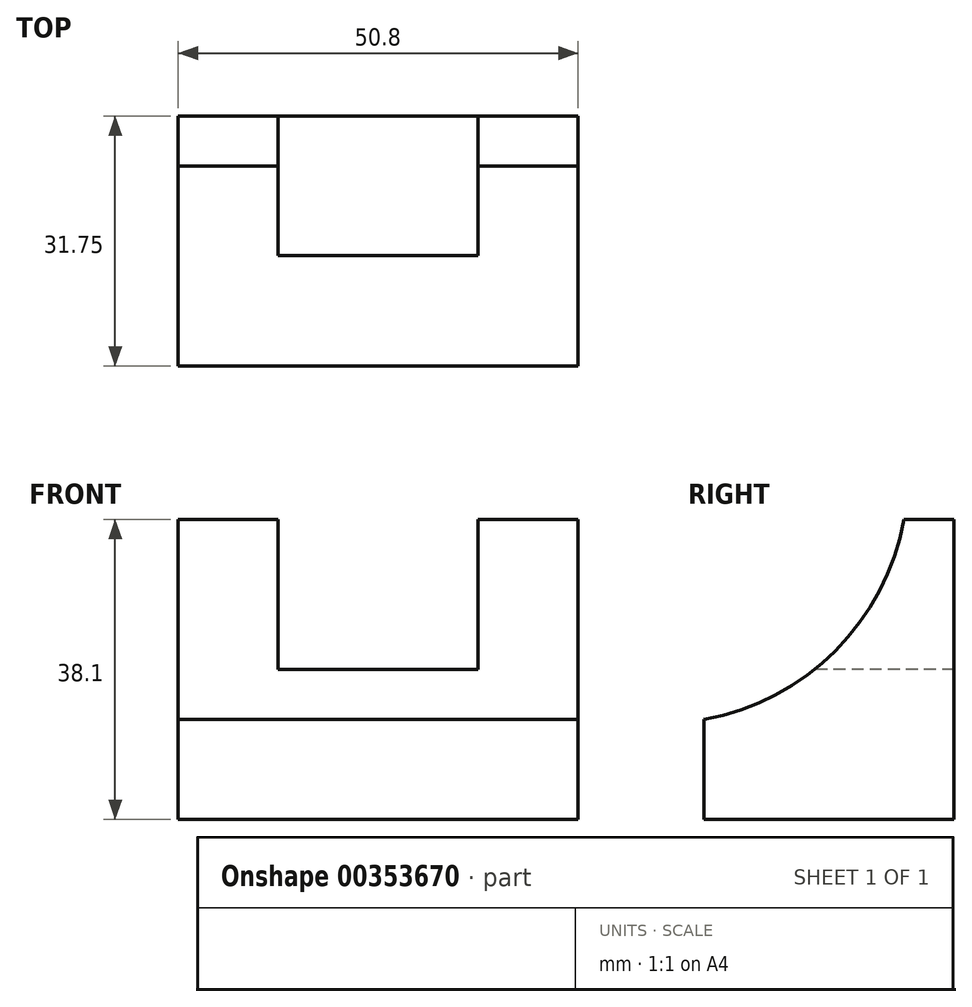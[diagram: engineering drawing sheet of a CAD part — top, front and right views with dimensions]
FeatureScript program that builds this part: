
annotation { "Feature Type Name" : "Feature", "Feature Type Description" : "" }
export const myFeature = defineFeature(function(context is Context, id is Id, definition is map)
    precondition{}
    {
        {
            var Q0;
            Q0=qCreatedBy(makeId("Right.planeOp"),FACE);
            var sketch = newSketch(context, id + "F0", { "sketchPlane" : qUnion([Q0])});
            skLineSegment(sketch, "E0", {"start": v(-28.04, 18.9) * mm, "end": v(-28.04, -19.2) * mm});
            skLineSegment(sketch, "E1", {"start": v(-28.04, -19.2) * mm, "end": v(3.71, -19.2) * mm});
            skLineSegment(sketch, "E2", {"start": v(3.71, -19.2) * mm, "end": v(3.71, 18.9) * mm});
            skLineSegment(sketch, "E3", {"start": v(3.71, 18.9) * mm, "end": v(-28.04, 18.9) * mm});
            skSolve(sketch);
        }
        {
            var Q0;
            Q0=makeQuery(id+"F0.imprint","IMPRINT",FACE,{"disambiguationData":[TD([[makeQuery(id+"F0.imprint","IMPRINT",EDGE,{"derivedFrom":sQuery(id+"F0.wireOp",EDGE,"E0")}),1.0]])]});
            extrude(context, id + "F1", {"entities" : qUnion([Q0]), "depth" : 50.8 * mm});
        }
        {
            var Q0;
            Q0=makeQuery(id+"F1.opExtrude","SWEPT_FACE",FACE,{"disambiguationData":[OSD([sQuery(id+"F0.wireOp",EDGE,"E0")])]});
            var sketch = newSketch(context, id + "F2", { "sketchPlane" : qUnion([Q0])});
            skLineSegment(sketch, "E4", {"start": v(12.7, 18.9) * mm, "end": v(12.7, -0.14) * mm});
            skLineSegment(sketch, "E5", {"start": v(12.7, -0.14) * mm, "end": v(38.1, -0.14) * mm});
            skLineSegment(sketch, "E6", {"start": v(38.1, -0.14) * mm, "end": v(38.1, 18.9) * mm});
            skSolve(sketch);
        }
        {
            var Q0;
            Q0 = qSketchRegion(id + "F2", true);
            var Q1;
            {var subQ0=sQuery(id+"F2.wireOp",EDGE,"E4");Q1=makeQuery(id+"F2.imprint","IMPRINT",FACE,{"disambiguationData":[TD([[makeQuery(id+"F2.imprint","IMPRINT",EDGE,{"derivedFrom":subQ0}),1.0]])]});}
            extrude(context, id + "F3", {"entities" : qUnion([Q0, Q1]), "operationType" : NewBodyOperationType.REMOVE, "oppositeDirection" : true, "depth" : 38.1 * mm});
        }
        {
            var Q0;
            Q0=makeQuery(id+"F1.opExtrude","CAP_FACE",FACE,{"disambiguationData":[OSD([sQuery(id+"F0.wireOp",EDGE,"E0"),sQuery(id+"F0.wireOp",EDGE,"E1"),sQuery(id+"F0.wireOp",EDGE,"E2"),sQuery(id+"F0.wireOp",EDGE,"E3")])],"isStart":false});
            var sketch = newSketch(context, id + "F4", { "sketchPlane" : qUnion([Q0])});
            skArc(sketch, "E7", {"start": v(-28.04, -6.5) * mm, "mid": v(-11.36, 2.24) * mm, "end": v(-2.64, 18.9) * mm});
            skSolve(sketch);
        }
        {
            var Q0;
            Q0 = qSketchRegion(id + "F4", true);
            var Q1;
            {var subQ0=sQuery(id+"F4.wireOp",EDGE,"E7");Q1=makeQuery(id+"F4.imprint","IMPRINT",FACE,{"disambiguationData":[TD([[makeQuery(id+"F4.imprint","IMPRINT",EDGE,{"derivedFrom":subQ0}),1.0]])]});}
            extrude(context, id + "F5", {"entities" : qUnion([Q0, Q1]), "operationType" : NewBodyOperationType.REMOVE, "oppositeDirection" : true, "depth" : 50.8 * mm});
        }
    });
